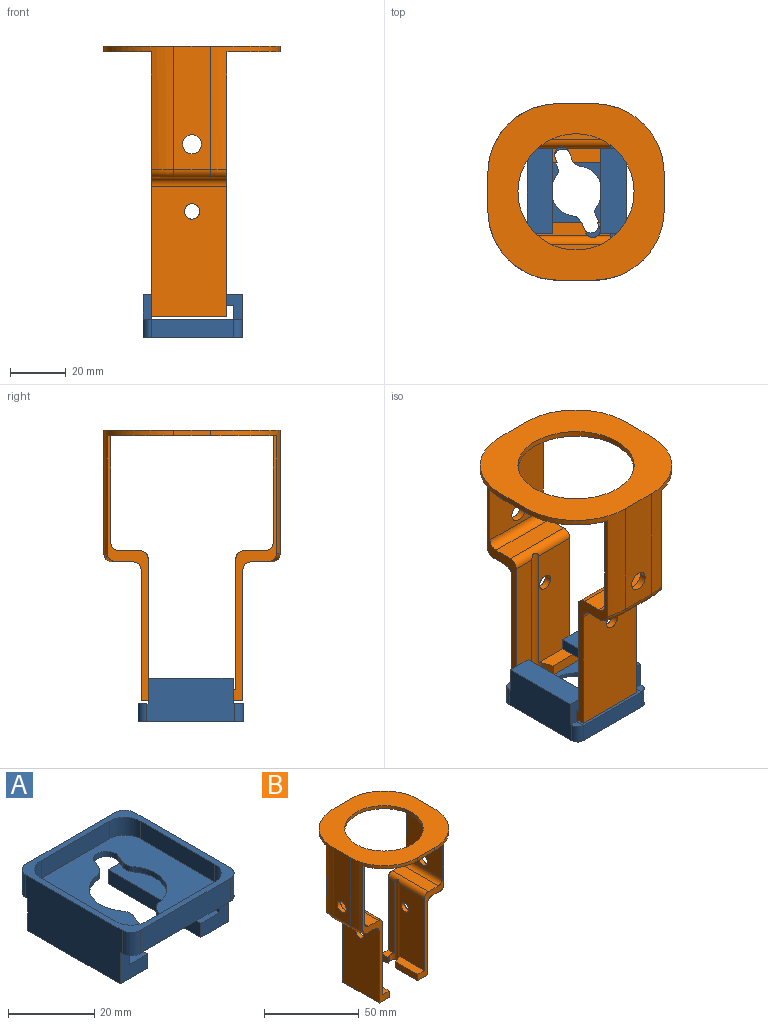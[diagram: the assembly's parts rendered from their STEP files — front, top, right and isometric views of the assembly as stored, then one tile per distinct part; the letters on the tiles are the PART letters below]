
ASSEMBLY  parts=2 mates=1
PART A: 45 faces, bbox 35.4x37.5x15.5 mm
  f0: plane 31.5x15.5mm, normal (-1,0,0), area 477.9mm2, adj f3,f8,f10,f18,f19,f28,f41,f42
  f1: plane 30.34x4mm, normal (1,0,0), area 121.4mm2, adj f3,f4,f19,f41
  f2: plane 30.34x4mm, normal (-1,0,0), area 121.4mm2, adj f6,f21,f22,f43
  f3: plane 30.34x9mm, normal (0,0,-1), area 273.1mm2, adj f0,f1,f19,f41
  f4: plane 30.34x6mm, normal (0,0,1), area 182mm2, adj f1,f5,f19,f41
  f5: plane 33.92x5mm, normal (1,0,0), area 152.1mm2, adj f4,f8,f10,f19,f41,f42
  f6: plane 30.34x9mm, normal (0,0,-1), area 273.1mm2, adj f2,f16,f22,f43
  f7: cylinder r=3mm len=6.6mm, axis (0,0,1), area 31.1mm2, adj f11,f16,f18,f20,f44
  f8: cylinder r=3mm len=6.6mm, axis (0,0,-1), area 31.1mm2, adj f0,f5,f11,f18,f42
  f9: plane 34.5x32.42mm, normal (0,0,1), area 762mm2, adj f12,f13,f14,f15,f23,f24,f25,f26
  f10: plane 37.5x35.42mm, normal (0,0,-1), area 785.9mm2, adj f0,f5,f11,f16,f17,f19,f20,f22
  f11: plane 29.42x6.5mm, normal (0,-1,0), area 191.2mm2, adj f7,f8,f10,f18
  f12: plane 22.42x5mm, normal (0,1,0), area 112.1mm2, adj f9,f18,f23,f24
  f13: plane 24.5x5mm, normal (-1,0,0), area 122.5mm2, adj f9,f18,f23,f26
  f14: plane 22.42x5mm, normal (0,-1,0), area 112.1mm2, adj f9,f18,f25,f26
  f15: plane 24.5x5mm, normal (1,0,0), area 122.5mm2, adj f9,f18,f24,f25
  f16: plane 31.5x15.5mm, normal (1,0,0), area 477.9mm2, adj f6,f7,f10,f18,f22,f27,f43,f44
  f17: plane 29.42x6.5mm, normal (0,1,0), area 191.2mm2, adj f10,f18,f27,f28
  f18: plane 37.5x35.42mm, normal (0,0,1), area 223.5mm2, adj f0,f7,f8,f11,f12,f13,f14,f15
  f19: plane 9x9mm, normal (0,1,0), area 51mm2, adj f0,f1,f3,f4,f5,f10
  f20: plane 33.92x5mm, normal (-1,0,0), area 152.1mm2, adj f7,f10,f21,f22,f43,f44
  f21: plane 30.34x6mm, normal (0,0,1), area 182mm2, adj f2,f20,f22,f43
  f22: plane 9x9mm, normal (0,1,0), area 51mm2, adj f2,f6,f10,f16,f20,f21
  f23: cylinder r=5mm len=5mm, axis (0,0,-1), area 39.3mm2, adj f9,f12,f13,f18
  f24: cylinder r=5mm len=5mm, axis (0,0,1), area 39.3mm2, adj f9,f12,f15,f18
  f25: cylinder r=5mm len=5mm, axis (0,0,-1), area 39.3mm2, adj f9,f14,f15,f18
  f26: cylinder r=5mm len=5mm, axis (0,0,1), area 39.3mm2, adj f9,f13,f14,f18
  f27: cylinder r=3mm len=6.5mm, axis (0,0,-1), area 30.6mm2, adj f10,f16,f17,f18
  f28: cylinder r=3mm len=6.5mm, axis (0,0,1), area 30.6mm2, adj f0,f10,f17,f18
  f29: plane 2.16x1.5mm, normal (0.92,-0.38,0), area 3.5mm2, adj f9,f10,f30,f40
  f30: cylinder r=3mm len=5.74mm, axis (0,0,-1), area 14.4mm2, adj f9,f10,f29,f31
  f31: plane 2.48x1.5mm, normal (-0.92,0.38,0), area 4mm2, adj f9,f10,f30,f37
  f32: cylinder r=9mm len=14.39mm, axis (0,0,-1), area 28.3mm2, adj f9,f10,f37,f38
  f33: plane 2.41x1.5mm, normal (-0.92,0.38,0), area 3.9mm2, adj f9,f10,f34,f38
  f34: cylinder r=3mm len=5.77mm, axis (0,0,-1), area 14.1mm2, adj f9,f10,f33,f35
  f35: plane 2.4x1.5mm, normal (0.92,-0.38,0), area 3.9mm2, adj f9,f10,f34,f39
  f36: cylinder r=9mm len=14.4mm, axis (0,0,-1), area 28.3mm2, adj f9,f10,f39,f40
  f37: cylinder r=3mm len=2.38mm, axis (0,0,-1), area 4.7mm2, adj f9,f10,f31,f32
  f38: cylinder r=3mm len=2.98mm, axis (0,0,-1), area 4.7mm2, adj f9,f10,f32,f33
  f39: cylinder r=3mm len=2.38mm, axis (0,0,-1), area 4.7mm2, adj f9,f10,f35,f36
  f40: cylinder r=3mm len=2.98mm, axis (0,0,-1), area 4.7mm2, adj f9,f10,f29,f36
  f41: plane 9x8.9mm, normal (0,-1,0), area 50.7mm2, adj f0,f1,f3,f4,f5,f42
  f42: plane 3.58x3mm, normal (0,0,-1), area 8.8mm2, adj f0,f5,f8,f41
  f43: plane 9x8.9mm, normal (0,-1,0), area 50.7mm2, adj f2,f6,f16,f20,f21,f44
  f44: plane 3.58x3mm, normal (0,0,-1), area 8.8mm2, adj f7,f16,f20,f43
PART B: 59 faces, bbox 63.9x63x96.6 mm
  f0: plane 46.6x4.88mm, normal (-1,0,0), area 227.3mm2, adj f8,f23,f50,f57
  f1: plane 46.6x18.88mm, normal (-1,0,0), area 856mm2, adj f21,f31,f37,f50,f57
  f2: plane 46.6x7.88mm, normal (1,0,0), area 367.1mm2, adj f18,f29,f52,f54
  f3: plane 46.6x15.88mm, normal (1,0,0), area 716.2mm2, adj f7,f19,f38,f52,f54
  f4: plane 13.46x4mm, normal (1,0,0), area 53.8mm2, adj f6,f7,f19,f55
  f5: plane 16.49x4mm, normal (-1,0,0), area 66mm2, adj f21,f28,f31,f58
  f6: plane 27x7.5mm, normal (0,0,-1), area 174.9mm2, adj f4,f18,f19,f26,f30,f53,f54,f55
  f7: plane 15.88x5mm, normal (0,0,1), area 72.5mm2, adj f3,f4,f19,f54,f55
  f8: plane 5x4.89mm, normal (0,0,1), area 21.1mm2, adj f0,f23,f32,f56,f57
  f9: plane 27x7.35mm, normal (0,0,-1), area 192.8mm2, adj f21,f23,f44,f45,f46,f47
  f10: plane 38x27mm, normal (1,0,0), area 989.7mm2, adj f16,f18,f19,f40,f51
  f11: plane 13x2mm, normal (0,-1,0), area 26mm2, adj f16,f17,f33,f36
  f12: plane 44x13mm, normal (1,0,0), area 535.7mm2, adj f17,f33,f34,f39,f45
  f13: plane 13x2mm, normal (0,1,0), area 26mm2, adj f16,f17,f34,f35
  f14: cylinder r=20.75mm len=41.5mm, axis (0,0,1), area 260.8mm2, adj f16,f17
  f15: plane 44x13mm, normal (-1,0,0), area 535.7mm2, adj f17,f35,f36,f40,f42
  f16: plane 63x61.54mm, normal (0,0,-1), area 1954.7mm2, adj f10,f11,f13,f14,f18,f19,f21,f22
  f17: plane 63x63mm, normal (0,0,1), area 2079.8mm2, adj f11,f12,f13,f14,f15,f33,f34,f35
  f18: plane 94.6x19.54mm, normal (0,-1,0), area 250.6mm2, adj f2,f6,f10,f16,f20,f24,f26,f29
  f19: plane 94.6x20.12mm, normal (0,1,0), area 277mm2, adj f3,f4,f6,f7,f10,f16,f20,f24
  f20: plane 27x7.35mm, normal (0,0,-1), area 192.8mm2, adj f18,f19,f41,f42,f43,f48
  f21: plane 94.6x19.54mm, normal (0,-1,0), area 250.6mm2, adj f1,f5,f9,f16,f22,f25,f27,f28
  f22: plane 38x27mm, normal (-1,0,0), area 989.7mm2, adj f16,f21,f23,f39,f49
  f23: plane 94.6x20.12mm, normal (0,1,0), area 277mm2, adj f0,f8,f9,f16,f22,f25,f27,f28
  f24: plane 27x7.35mm, normal (0,0,1), area 198.4mm2, adj f18,f19,f51,f52
  f25: plane 27x7.35mm, normal (0,0,1), area 198.4mm2, adj f21,f23,f49,f50
  f26: plane 46.6x27mm, normal (-1,0,0), area 1234.5mm2, adj f6,f18,f19,f38,f48
  f27: plane 46.6x27mm, normal (1,0,0), area 1234.5mm2, adj f21,f23,f28,f37,f47
  f28: plane 27x7.5mm, normal (0,0,-1), area 175mm2, adj f5,f21,f23,f27,f32,f56,f57,f58
  f29: plane 7.88x5mm, normal (0,0,1), area 36.1mm2, adj f2,f18,f30,f53,f54
  f30: plane 7.82x4mm, normal (1,0,0), area 31.3mm2, adj f6,f18,f29,f53
  f31: plane 18.88x5mm, normal (0,0,1), area 87.6mm2, adj f1,f5,f21,f57,f58
  f32: plane 4.89x4mm, normal (-1,0,0), area 19.6mm2, adj f8,f23,f28,f56
  f33: cylinder r=25mm len=44mm, axis (0,0,-1), area 420.6mm2, adj f11,f12,f16,f17,f21,f46
  f34: cylinder r=25mm len=44mm, axis (0,0,1), area 333mm2, adj f12,f13,f16,f17,f23,f44
  f35: cylinder r=25mm len=44mm, axis (0,0,-1), area 333mm2, adj f13,f15,f16,f17,f19,f41
  f36: cylinder r=25mm len=44mm, axis (0,0,1), area 420.6mm2, adj f11,f15,f16,f17,f18,f43
  f37: cylinder r=2.75mm len=5.5mm, axis (1,0,0), area 43.2mm2, adj f1,f27
  f38: cylinder r=2.75mm len=5.5mm, axis (1,0,0), area 43.2mm2, adj f3,f26
  f39: cylinder r=3.4mm len=6.8mm, axis (1,0,0), area 53.4mm2, adj f12,f22
  f40: cylinder r=3.4mm len=6.8mm, axis (1,0,0), area 53.4mm2, adj f10,f15
  f41: torus R=22mm, axis (0,0,-1), area 28.6mm2, adj f19,f20,f35,f42
  f42: cylinder r=3mm len=13mm, axis (0,-1,0), area 61.3mm2, adj f15,f20,f41,f43
  f43: torus R=22mm, axis (0,0,-1), area 38.4mm2, adj f18,f20,f36,f42
  f44: torus R=22mm, axis (0,0,-1), area 28.6mm2, adj f9,f23,f34,f45
  f45: cylinder r=3mm len=13mm, axis (0,1,0), area 61.3mm2, adj f9,f12,f44,f46
  f46: torus R=22mm, axis (0,0,-1), area 38.4mm2, adj f9,f21,f33,f45
  f47: cylinder r=3mm len=27mm, axis (0,-1,0), area 127.2mm2, adj f9,f21,f23,f27
  f48: cylinder r=3mm len=27mm, axis (0,1,0), area 127.2mm2, adj f18,f19,f20,f26
  f49: cylinder r=3mm len=27mm, axis (0,-1,0), area 127.2mm2, adj f21,f22,f23,f25
  f50: cylinder r=3mm len=27mm, axis (0,-1,0), area 122.5mm2, adj f0,f1,f21,f23,f25,f57
  f51: cylinder r=3mm len=27mm, axis (0,-1,0), area 127.2mm2, adj f10,f18,f19,f24
  f52: cylinder r=3mm len=27mm, axis (0,1,0), area 122.5mm2, adj f2,f3,f18,f19,f24,f54
  f53: plane 4x1.91mm, normal (-0.38,0.93,0), area 8.2mm2, adj f6,f29,f30,f54
  f54: cylinder r=2.65mm len=52.34mm, axis (0,0,-1), area 200.7mm2, adj f2,f3,f6,f7,f29,f52,f53,f55
  f55: plane 4x3.9mm, normal (0.38,-0.93,0), area 16.8mm2, adj f4,f6,f7,f54
  f56: plane 4x1.91mm, normal (0.4,-0.91,0), area 8.3mm2, adj f8,f28,f32,f57
  f57: cylinder r=2.65mm len=52.34mm, axis (0,0,-1), area 200.7mm2, adj f0,f1,f8,f28,f31,f50,f56,f58
  f58: plane 4x3.9mm, normal (-0.37,0.93,0), area 16.8mm2, adj f5,f28,f31,f57
PLACE A rot(axis=(0,1,0),180deg) t=(-20.48,0.67,-122.43)mm
PLACE B rot(axis=(0,0,-1),90deg) t=(-20.69,0.19,-24.83)mm
MATE fastened A.f22 <-> B.f2  axis (0,-1,0) through (-35.19,15.84,-117.43)mm
